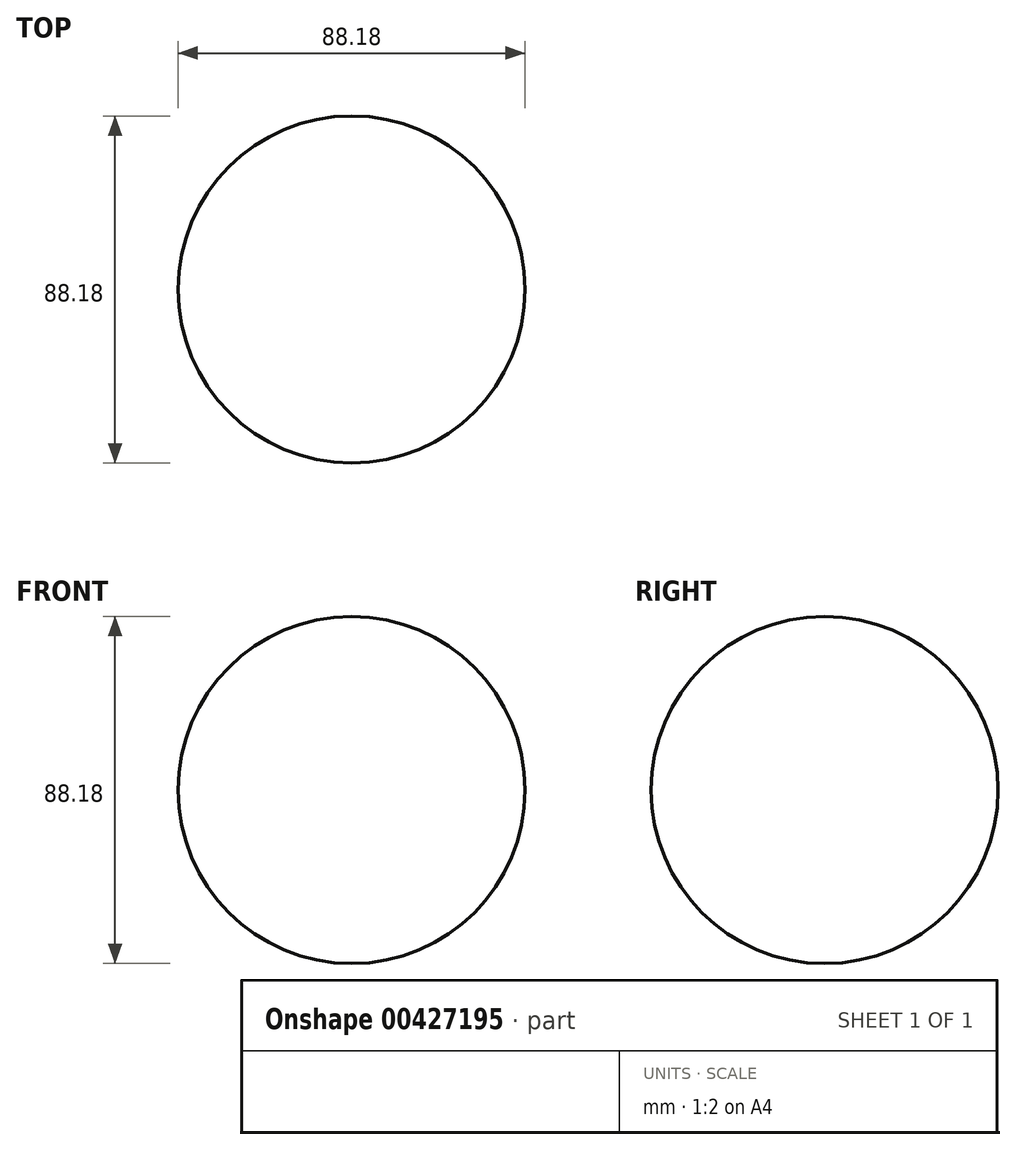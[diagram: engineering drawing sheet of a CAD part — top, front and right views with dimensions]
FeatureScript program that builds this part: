
annotation { "Feature Type Name" : "Feature", "Feature Type Description" : "" }
export const myFeature = defineFeature(function(context is Context, id is Id, definition is map)
    precondition{}
    {
        {
            var Q0;
            Q0=qCreatedBy(makeId("Front.planeOp"),FACE);
            var sketch = newSketch(context, id + "F0", { "sketchPlane" : qUnion([Q0])});
            skArc(sketch, "E0", {"start": v(0, 44.09) * mm, "mid": v(-44.09, 0) * mm, "end": v(0, -44.09) * mm});
            skLineSegment(sketch, "E1", {"start": v(0, 44.09) * mm, "end": v(0, -44.09) * mm});
            skLineSegment(sketch, "E2", {"start": v(0, 0) * mm, "end": v(0, 56.6) * mm, "construction": true});
            skSolve(sketch);
        }
        {
            var Q0;
            Q0=makeQuery(id+"F0.imprint","IMPRINT",FACE,{"disambiguationData":[TD([[makeQuery(id+"F0.imprint","IMPRINT",EDGE,{"derivedFrom":sQuery(id+"F0.wireOp",EDGE,"E0")}),1.0]])]});
            var Q1;
            Q1=sQuery(id+"F0.wireOp",EDGE,"E2");
            revolve(context, id + "F1", {"entities" : qUnion([Q0]), "axis" : qUnion([Q1]), "revolveType" : RevolveType.FULL});
        }
    });
